# Revit family: 248465xx0--Sanitary_Bath-Spas_Roca_BEYOND-SURFEXR-oval-bathtub-with-drain
name_source: partatom
category: Plumbing Fixtures
units: mm (PartAtom-declared; Revit-internal decimal feet)

## family parameters
Always vertical = No
Cut with Voids When Loaded = No
OmniClass Number = 23.31.15.11
Part Type = Normal
Room Calculation Point = No
Round Connector Dimension = Use Diameter
Shared = No
Work Plane-Based = No

## types (1)
- BEYOND SURFEX oval bathtub with drain
    BIMobject category = Bath & Spas
    BIMobject category code = sanitary-bath-spas
    BIMobject main category = Sanitary
    BIMobject main category code = sanitary
    Brand url = http://www.roca.com
    Design country = Spain
    Edition number = 1
    IFC Classification = Sanitary Terminal
    Manufacturer country = Spain
    Manufacturer name = Roca
    Masterformat 2014 Code = 22 41 19
    Masterformat 2014 Description = Residential Bathtubs
    Material main = Solid surface
    NBS Reference Code = 35-06-08
    NBS Reference Description = Baths
    OmniClass Code = 23-31 15 11
    OmniClass Description = Bath Shower Units
    Product Guid = fdef3261-2f4a-4fb8-8813-17919ae72857
    Product SKU = 248465xx0
    Product data url = https://bimobject.com
    Product family = Beyond
    Product group = Bath
    Product name = BEYOND SURFEX® oval bathtub with drain
    Product url = http://www.roca.com
    QR code = https://www.roca.com
    Technical description = http://www.roca.com
    Uniclass 1.4 Code = L7211
    Uniclass 1.4 Description = Baths
    Uniclass 2.0 Code = PR-35-06-08
    Uniclass 2.0 Description = Baths
    Uniclass 2015 Code = Pr_40_20_06_08
    Uniclass 2015 Name = Baths
    Uniformat II Code = D2010
    Uniformat II Description = Plumbing Fixtures
    Youtube clip = https://www.youtube.com

## geometry (parser evidence)
native form markers: Blend x4, Sweep x2
no freeform markers — native parametric forms only
